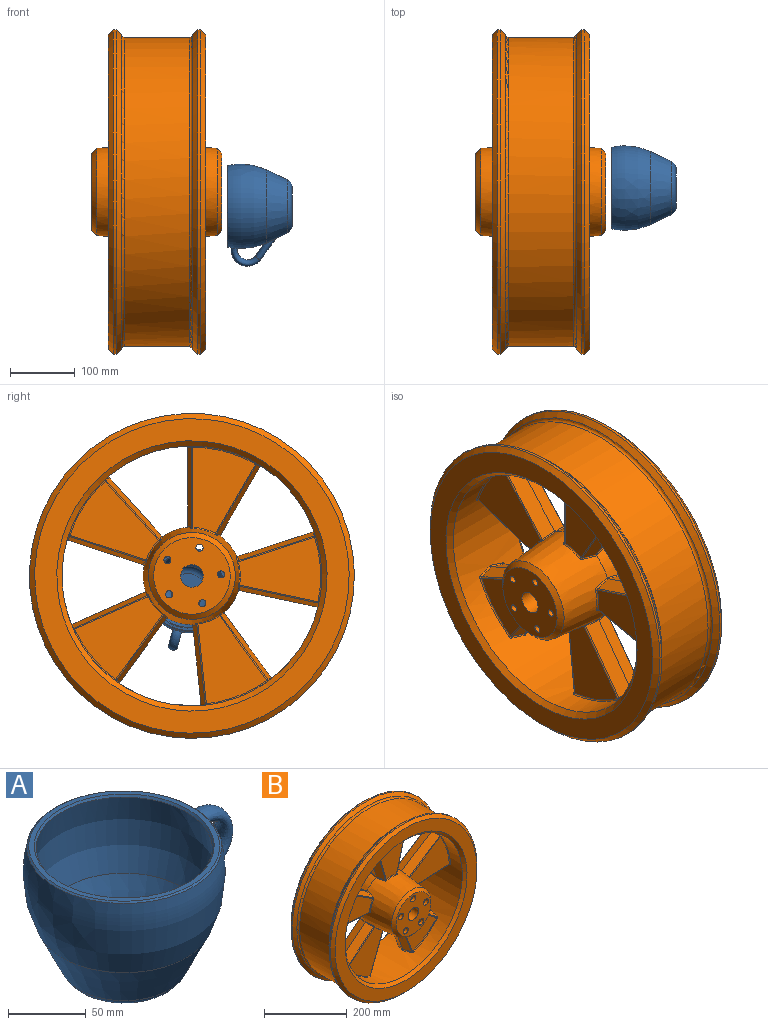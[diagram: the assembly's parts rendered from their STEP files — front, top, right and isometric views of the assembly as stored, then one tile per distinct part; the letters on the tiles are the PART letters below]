
ASSEMBLY  parts=2 mates=1
PART A: 13 faces, bbox 160.1x130.2x100 mm
  f0: revolved ~130.2x130.2mm, area 23793.2mm2, adj f3,f4,f5,f12
  f1: plane 122.99x122.99mm, normal (0,0,1), area 1330.6mm2, adj f11,f12
  f2: plane 59.81x59.81mm, normal (0,0,-1), area 2809.6mm2, adj f10
  f3: cone r=37.5mm half-angle=25.3deg, axis (0,0,1), area 10977.2mm2, adj f0,f4,f10
  f4: bspline ~41.94x33.4mm, area 1363.5mm2, adj f0,f3,f5
  f5: bspline ~45.43x33.49mm, area 2154.2mm2, adj f0,f4
  f6: revolved ~118.2x118.2mm, area 20523.6mm2, adj f8,f11
  f7: plane 52.22x52.22mm, normal (0,0,1), area 2141.3mm2, adj f9
  f8: cone r=33.7mm half-angle=25.3deg, axis (0,0,1), area 9083.2mm2, adj f6,f9
  f9: torus R=26.11mm, axis (0,0,1), area 2739mm2, adj f7,f8
  f10: torus R=29.91mm, axis (0,0,-1), area 3062.2mm2, adj f2,f3
  f11: cone r=56.71mm half-angle=38.1deg, axis (0,0,1), area 722.7mm2, adj f1,f6
  f12: cone r=62.74mm half-angle=51.6deg, axis (0,0,-1), area 618.7mm2, adj f0,f1
PART B: 186 faces, bbox 547x222x547 mm
  f0: cylinder r=250mm len=500mm, axis (0,1,0), area 6283.2mm2, adj f1,f185
  f1: cone r=250mm half-angle=45deg, axis (0,-1,0), area 17487.2mm2, adj f0,f2
  f2: plane 484x484mm, normal (0,1,0), area 48066.4mm2, adj f1,f3
  f3: cone r=208mm half-angle=45deg, axis (0,1,0), area 14501.6mm2, adj f2,f4
  f4: cylinder r=200mm len=400mm, axis (0,1,0), area 137396.1mm2, adj f3,f5,f128,f129,f130,f131,f132,f133
  f5: bspline ~4.6x3.93mm, area 11.3mm2, adj f4,f6,f128,f136
  f6: cylinder r=2mm len=119.66mm, axis (-0.26,0,-0.97), area 322.6mm2, adj f5,f7,f126,f127
  f7: plane 125.52x99.52mm, normal (0,1,0), area 8426.2mm2, adj f6,f8,f125,f128
  f8: cylinder r=2mm len=119.66mm, axis (-0.26,0,0.97), area 322.6mm2, adj f7,f9,f124,f129
  f9: plane 119x37.91mm, normal (-0.93,0.26,-0.25), area 2975.3mm2, adj f8,f10,f123,f130
  f10: plane 119x37.91mm, normal (-0.93,-0.26,-0.25), area 2975.3mm2, adj f9,f11,f122,f131
  f11: cylinder r=2mm len=119.66mm, axis (-0.26,0,0.97), area 322.6mm2, adj f10,f12,f121,f132
  f12: plane 125.52x99.52mm, normal (0,-1,0), area 8426.2mm2, adj f11,f13,f120,f133
  f13: cylinder r=2mm len=119.66mm, axis (-0.26,0,-0.97), area 322.6mm2, adj f12,f14,f119,f134
  f14: plane 119x37.91mm, normal (0.93,-0.26,-0.25), area 2975.3mm2, adj f13,f15,f127,f135
  f15: bspline ~24.26x7.79mm, area 72.3mm2, adj f14,f16,f118,f119
  f16: cone r=75mm half-angle=5deg, axis (0,1,0), area 34978.1mm2, adj f15,f17,f33,f34,f35,f36,f37,f53
  f17: bspline ~24.26x7.69mm, area 72.3mm2, adj f16,f18,f32,f33
  f18: plane 117.04x49.43mm, normal (0.9,-0.26,-0.35), area 2975.3mm2, adj f17,f19,f31,f150
  f19: cylinder r=2mm len=115.86mm, axis (-0.36,0,-0.93), area 322.6mm2, adj f18,f20,f33,f151
  f20: plane 136.13x124.73mm, normal (0,-1,0), area 8426.2mm2, adj f19,f21,f34,f152
  f21: cylinder r=2mm len=97.09mm, axis (0.78,0,0.63), area 322.6mm2, adj f20,f22,f35,f153
  f22: plane 99.51x81.37mm, normal (-0.61,-0.26,0.75), area 2975.3mm2, adj f21,f23,f36,f154
  f23: plane 99.51x81.37mm, normal (-0.61,0.26,0.75), area 2975.3mm2, adj f22,f24,f30,f155
  f24: cylinder r=2mm len=97.09mm, axis (0.78,0,0.63), area 322.6mm2, adj f23,f25,f29,f156
  f25: plane 136.13x124.73mm, normal (0,1,0), area 8426.2mm2, adj f24,f26,f28,f147
  f26: cylinder r=2mm len=115.86mm, axis (-0.36,0,-0.93), area 322.6mm2, adj f25,f27,f31,f148
  f27: bspline ~4.46x3.93mm, area 10.7mm2, adj f26,f28,f32,f77
  f28: torus R=74.65mm, axis (0,1,0), area 105.1mm2, adj f25,f27,f29,f77
  f29: bspline ~4.44x3.65mm, area 10.7mm2, adj f24,f28,f30,f77
  f30: bspline ~24.26x6.52mm, area 72.3mm2, adj f23,f29,f36,f77
  f31: plane 117.04x49.43mm, normal (0.9,0.26,-0.35), area 2975.3mm2, adj f18,f26,f32,f149
  f32: bspline ~24.26x7.69mm, area 72.3mm2, adj f17,f27,f31,f77
  f33: bspline ~4.66x3.65mm, area 10.7mm2, adj f16,f17,f19,f34
  f34: torus R=74.65mm, axis (0,-1,0), area 105.1mm2, adj f16,f20,f33,f35
  f35: bspline ~4.27x3.93mm, area 10.7mm2, adj f16,f21,f34,f36
  f36: bspline ~24.26x6.52mm, area 72.3mm2, adj f16,f22,f30,f35
  f37: bspline ~24.26x8.11mm, area 72.3mm2, adj f16,f38,f52,f53
  f38: plane 123.1x23.52mm, normal (-0.05,-0.26,-0.96), area 2975.3mm2, adj f37,f39,f51,f140
  f39: cylinder r=2mm len=123.3mm, axis (-1,0,0.05), area 322.6mm2, adj f38,f40,f53,f141
  f40: plane 134.22x101.11mm, normal (0,-1,0), area 8426.2mm2, adj f39,f41,f54,f142
  f41: cylinder r=2mm len=104.51mm, axis (0.84,0,-0.54), area 322.6mm2, adj f40,f42,f55,f143
  f42: plane 105.34x72.24mm, normal (0.53,-0.26,0.81), area 2975.3mm2, adj f41,f43,f56,f144
  f43: plane 105.34x72.24mm, normal (0.53,0.26,0.81), area 2975.3mm2, adj f42,f44,f50,f145
  f44: cylinder r=2mm len=104.51mm, axis (0.84,0,-0.54), area 322.6mm2, adj f43,f45,f49,f146
  f45: plane 134.22x101.11mm, normal (0,1,0), area 8426.2mm2, adj f44,f46,f48,f137
  f46: cylinder r=2mm len=123.3mm, axis (-1,0,0.05), area 322.6mm2, adj f45,f47,f51,f138
  f47: bspline ~4.26x3.93mm, area 10.7mm2, adj f46,f48,f52,f77
  f48: torus R=74.65mm, axis (0,1,0), area 105.1mm2, adj f45,f47,f49,f77
  f49: bspline ~4.11x3.79mm, area 10.7mm2, adj f44,f48,f50,f77
  f50: bspline ~24.26x6.91mm, area 72.3mm2, adj f43,f49,f56,f77
  f51: plane 123.1x23.52mm, normal (-0.05,0.26,-0.96), area 2975.3mm2, adj f38,f46,f52,f139
  f52: bspline ~24.26x8.11mm, area 72.3mm2, adj f37,f47,f51,f77
  f53: bspline ~4.69x3.65mm, area 10.7mm2, adj f16,f37,f39,f54
  f54: torus R=74.65mm, axis (0,-1,0), area 105.1mm2, adj f16,f40,f53,f55
  f55: bspline ~3.93x3.76mm, area 10.7mm2, adj f16,f41,f54,f56
  f56: bspline ~24.26x6.91mm, area 72.3mm2, adj f16,f42,f50,f55
  f57: bspline ~24.26x6.91mm, area 72.3mm2, adj f16,f58,f72,f73
  f58: plane 105.34x72.24mm, normal (-0.53,-0.26,0.81), area 2975.3mm2, adj f57,f59,f71,f170
  f59: cylinder r=2mm len=104.51mm, axis (0.84,0,0.54), area 322.6mm2, adj f58,f60,f73,f171
  f60: plane 134.22x101.11mm, normal (0,-1,0), area 8426.2mm2, adj f59,f61,f74,f172
  f61: cylinder r=2mm len=123.3mm, axis (-1,0,-0.05), area 322.6mm2, adj f60,f62,f75,f173
  f62: plane 123.1x23.52mm, normal (0.05,-0.26,-0.96), area 2975.3mm2, adj f61,f63,f76,f174
  f63: plane 123.1x23.52mm, normal (0.05,0.26,-0.96), area 2975.3mm2, adj f62,f64,f70,f175
  f64: cylinder r=2mm len=123.3mm, axis (-1,0,-0.05), area 322.6mm2, adj f63,f65,f69,f176
  f65: plane 134.22x101.11mm, normal (0,1,0), area 8426.2mm2, adj f64,f66,f68,f167
  f66: cylinder r=2mm len=104.51mm, axis (0.84,0,0.54), area 322.6mm2, adj f65,f67,f71,f168
  f67: bspline ~3.93x3.76mm, area 10.7mm2, adj f66,f68,f72,f77
  f68: torus R=74.65mm, axis (0,1,0), area 105.1mm2, adj f65,f67,f69,f77
  f69: bspline ~4.69x3.65mm, area 10.7mm2, adj f64,f68,f70,f77
  f70: bspline ~24.26x8.11mm, area 72.3mm2, adj f63,f69,f76,f77
  f71: plane 105.34x72.24mm, normal (-0.53,0.26,0.81), area 2975.3mm2, adj f58,f66,f72,f169
  f72: bspline ~24.26x6.91mm, area 72.3mm2, adj f57,f67,f71,f77
  f73: bspline ~4.11x3.79mm, area 10.7mm2, adj f16,f57,f59,f74
  f74: torus R=74.65mm, axis (0,-1,0), area 105.1mm2, adj f16,f60,f73,f75
  f75: bspline ~4.26x3.93mm, area 10.7mm2, adj f16,f61,f74,f76
  f76: bspline ~24.26x8.11mm, area 72.3mm2, adj f16,f62,f70,f75
  f77: cone r=75mm half-angle=5deg, axis (0,-1,0), area 34978.1mm2, adj f16,f27,f28,f29,f30,f32,f47,f48
  f78: bspline ~24.26x7.69mm, area 72.3mm2, adj f77,f79,f89,f116
  f79: plane 117.04x49.43mm, normal (-0.9,0.26,-0.35), area 2975.3mm2, adj f78,f80,f88,f165
  f80: cylinder r=2mm len=115.86mm, axis (-0.36,0,0.93), area 322.6mm2, adj f79,f81,f89,f166
  f81: plane 136.13x124.73mm, normal (0,1,0), area 8426.2mm2, adj f80,f82,f90,f157
  f82: cylinder r=2mm len=97.09mm, axis (0.78,0,-0.63), area 322.6mm2, adj f81,f83,f91,f158
  f83: plane 99.51x81.37mm, normal (0.61,0.26,0.75), area 2975.3mm2, adj f82,f84,f92,f159
  f84: plane 99.51x81.37mm, normal (0.61,-0.26,0.75), area 2975.3mm2, adj f83,f85,f112,f160
  f85: cylinder r=2mm len=97.09mm, axis (0.78,0,-0.63), area 322.6mm2, adj f84,f86,f113,f161
  f86: plane 136.13x124.73mm, normal (0,-1,0), area 8426.2mm2, adj f85,f87,f114,f162
  f87: cylinder r=2mm len=115.86mm, axis (-0.36,0,0.93), area 322.6mm2, adj f86,f88,f115,f163
  f88: plane 117.04x49.43mm, normal (-0.9,-0.26,-0.35), area 2975.3mm2, adj f79,f87,f116,f164
  f89: bspline ~4.66x3.65mm, area 10.7mm2, adj f77,f78,f80,f90
  f90: torus R=74.65mm, axis (0,1,0), area 105.1mm2, adj f77,f81,f89,f91
  f91: bspline ~4.27x3.93mm, area 10.7mm2, adj f77,f82,f90,f92
  f92: bspline ~24.26x6.52mm, area 72.3mm2, adj f77,f83,f91,f112
  f93: cone r=66.89mm half-angle=47.5deg, axis (0,-1,0), area 4272.4mm2, adj f77,f94
  f94: plane 139.84x139.84mm, normal (0,1,0), area 9469.1mm2, adj f93,f95,f107,f108,f109,f110,f111
  f95: cylinder r=17.5mm len=200mm, axis (0,-1,0), area 21991.1mm2, adj f94,f96
  f96: plane 117.84x117.84mm, normal (0,-1,0), area 8775.8mm2, adj f95,f97,f99,f101,f103,f105,f117
  f97: cylinder r=8.62mm len=17.25mm, axis (0,-1,0), area 541.9mm2, adj f96,f98
  f98: plane 17.25x17.25mm, normal (0,-1,0), area 138.7mm2, adj f97,f107
  f99: cylinder r=8.62mm len=17.25mm, axis (0,-1,0), area 541.9mm2, adj f96,f100
  f100: plane 17.25x17.25mm, normal (0,-1,0), area 138.7mm2, adj f99,f108
  f101: cylinder r=8.62mm len=17.25mm, axis (0,-1,0), area 541.9mm2, adj f96,f102
  f102: plane 17.25x17.25mm, normal (0,-1,0), area 138.7mm2, adj f101,f109
  f103: cylinder r=8.62mm len=17.25mm, axis (0,-1,0), area 541.9mm2, adj f96,f104
  f104: plane 17.25x17.25mm, normal (0,-1,0), area 138.7mm2, adj f103,f110
  f105: cylinder r=8.62mm len=17.25mm, axis (0,-1,0), area 541.9mm2, adj f96,f106
  f106: plane 17.25x17.25mm, normal (0,-1,0), area 138.7mm2, adj f105,f111
  f107: cylinder r=5.5mm len=190mm, axis (0,-1,0), area 6565.9mm2, adj f94,f98
  f108: cylinder r=5.5mm len=190mm, axis (0,-1,0), area 13131.9mm2, adj f94,f100
  f109: cylinder r=5.5mm len=190mm, axis (0,-1,0), area 6565.9mm2, adj f94,f102
  f110: cylinder r=5.5mm len=190mm, axis (0,-1,0), area 6565.9mm2, adj f94,f104
  f111: cylinder r=5.5mm len=190mm, axis (0,-1,0), area 6565.9mm2, adj f94,f106
  f112: bspline ~24.26x6.52mm, area 72.3mm2, adj f16,f84,f92,f113
  f113: bspline ~4.44x3.65mm, area 10.7mm2, adj f16,f85,f112,f114
  f114: torus R=74.65mm, axis (0,-1,0), area 105.1mm2, adj f16,f86,f113,f115
  f115: bspline ~4.46x3.93mm, area 10.7mm2, adj f16,f87,f114,f116
  f116: bspline ~24.26x7.69mm, area 72.3mm2, adj f16,f78,f88,f115
  f117: cone r=58.92mm half-angle=47.5deg, axis (0,1,0), area 4272.4mm2, adj f16,f96
  f118: bspline ~24.26x7.79mm, area 72.3mm2, adj f15,f77,f126,f127
  f119: bspline ~4.22x3.93mm, area 10.7mm2, adj f13,f15,f16,f120
  f120: torus R=74.65mm, axis (0,-1,0), area 105.1mm2, adj f12,f16,f119,f121
  f121: bspline ~4.63x3.65mm, area 10.7mm2, adj f11,f16,f120,f122
  f122: bspline ~24.26x7.79mm, area 72.3mm2, adj f10,f16,f121,f123
  f123: bspline ~24.26x7.79mm, area 72.3mm2, adj f9,f77,f122,f124
  f124: bspline ~4.22x3.93mm, area 10.7mm2, adj f8,f77,f123,f125
  f125: torus R=74.65mm, axis (0,1,0), area 105.1mm2, adj f7,f77,f124,f126
  f126: bspline ~4.63x3.65mm, area 10.7mm2, adj f6,f77,f118,f125
  f127: plane 119x37.91mm, normal (0.93,0.26,-0.25), area 2975.3mm2, adj f6,f14,f118,f136
  f128: torus R=198mm, axis (0,1,0), area 318.1mm2, adj f4,f5,f7,f129
  f129: bspline ~4.79x3.68mm, area 11.3mm2, adj f4,f8,f128,f130
  f130: bspline ~81.1x23.21mm, area 78.6mm2, adj f4,f9,f129,f131
  f131: bspline ~81.1x23.21mm, area 78.6mm2, adj f4,f10,f130,f132
  f132: bspline ~4.6x3.93mm, area 11.3mm2, adj f4,f11,f131,f133
  f133: torus R=198mm, axis (0,-1,0), area 318.1mm2, adj f4,f12,f132,f134
  f134: bspline ~4.79x3.68mm, area 11.3mm2, adj f4,f13,f133,f135
  f135: bspline ~81.1x23.21mm, area 78.6mm2, adj f4,f14,f134,f136
  f136: bspline ~81.1x23.21mm, area 78.6mm2, adj f4,f5,f127,f135
  f137: torus R=198mm, axis (0,1,0), area 318.1mm2, adj f4,f45,f138,f146
  f138: bspline ~4.89x3.68mm, area 11.3mm2, adj f4,f46,f137,f139
  f139: bspline ~81.1x23.7mm, area 78.6mm2, adj f4,f51,f138,f140
  f140: bspline ~81.1x23.7mm, area 78.6mm2, adj f4,f38,f139,f141
  f141: bspline ~4.43x3.93mm, area 11.3mm2, adj f4,f39,f140,f142
  f142: torus R=198mm, axis (0,-1,0), area 318.1mm2, adj f4,f40,f141,f143
  f143: bspline ~4.8x3.68mm, area 11.3mm2, adj f4,f41,f142,f144
  f144: bspline ~81.1x20.57mm, area 78.6mm2, adj f4,f42,f143,f145
  f145: bspline ~81.1x20.57mm, area 78.6mm2, adj f4,f43,f144,f146
  f146: bspline ~4.56x3.6mm, area 11.3mm2, adj f4,f44,f137,f145
  f147: torus R=198mm, axis (0,1,0), area 318.1mm2, adj f4,f25,f148,f156
  f148: bspline ~4.57x3.68mm, area 11.3mm2, adj f4,f26,f147,f149
  f149: bspline ~24.55x7.38mm, area 78.6mm2, adj f4,f31,f148,f150
  f150: bspline ~24.55x7.38mm, area 78.6mm2, adj f4,f18,f149,f151
  f151: bspline ~4.07x3.6mm, area 11.3mm2, adj f4,f19,f150,f152
  f152: torus R=198mm, axis (0,-1,0), area 318.1mm2, adj f4,f20,f151,f153
  f153: bspline ~4.34x3.8mm, area 11.3mm2, adj f4,f21,f152,f154
  f154: bspline ~81.1x18.84mm, area 78.6mm2, adj f4,f22,f153,f155
  f155: bspline ~81.1x18.84mm, area 78.6mm2, adj f4,f23,f154,f156
  f156: bspline ~4.21x3.93mm, area 11.3mm2, adj f4,f24,f147,f155
  f157: torus R=198mm, axis (0,1,0), area 318.1mm2, adj f4,f81,f158,f166
  f158: bspline ~4.34x3.8mm, area 11.3mm2, adj f4,f82,f157,f159
  f159: bspline ~81.1x18.84mm, area 78.6mm2, adj f4,f83,f158,f160
  f160: bspline ~81.1x18.84mm, area 78.6mm2, adj f4,f84,f159,f161
  f161: bspline ~4.21x3.93mm, area 11.3mm2, adj f4,f85,f160,f162
  f162: torus R=198mm, axis (0,-1,0), area 318.1mm2, adj f4,f86,f161,f163
  f163: bspline ~4.57x3.68mm, area 11.3mm2, adj f4,f87,f162,f164
  f164: bspline ~24.55x7.38mm, area 78.6mm2, adj f4,f88,f163,f165
  f165: bspline ~24.55x7.38mm, area 78.6mm2, adj f4,f79,f164,f166
  f166: bspline ~4.07x3.6mm, area 11.3mm2, adj f4,f80,f157,f165
  f167: torus R=198mm, axis (0,1,0), area 318.1mm2, adj f4,f65,f168,f176
  f168: bspline ~4.8x3.68mm, area 11.3mm2, adj f4,f66,f167,f169
  f169: bspline ~81.1x20.57mm, area 78.6mm2, adj f4,f71,f168,f170
  f170: bspline ~81.1x20.57mm, area 78.6mm2, adj f4,f58,f169,f171
  f171: bspline ~4.56x3.6mm, area 11.3mm2, adj f4,f59,f170,f172
  f172: torus R=198mm, axis (0,-1,0), area 318.1mm2, adj f4,f60,f171,f173
  f173: bspline ~4.89x3.68mm, area 11.3mm2, adj f4,f61,f172,f174
  f174: bspline ~81.1x23.7mm, area 78.6mm2, adj f4,f62,f173,f175
  f175: bspline ~81.1x23.7mm, area 78.6mm2, adj f4,f63,f174,f176
  f176: bspline ~4.43x3.93mm, area 11.3mm2, adj f4,f64,f167,f175
  f177: cone r=200mm half-angle=45deg, axis (0,-1,0), area 14501.6mm2, adj f4,f178
  f178: plane 484x484mm, normal (0,-1,0), area 48066.4mm2, adj f177,f179
  f179: cone r=242mm half-angle=45deg, axis (0,1,0), area 17487.2mm2, adj f178,f180
  f180: cylinder r=250mm len=500mm, axis (0,1,0), area 6283.2mm2, adj f179,f181
  f181: cone r=250mm half-angle=45deg, axis (0,-1,0), area 17487.2mm2, adj f180,f182
  f182: torus R=242.5mm, axis (0,-1,0), area 11047.5mm2, adj f181,f183
  f183: cylinder r=237.5mm len=475mm, axis (0,1,0), area 149300.5mm2, adj f182,f184
  f184: torus R=242.5mm, axis (0,1,0), area 11047.5mm2, adj f183,f185
  f185: cone r=242mm half-angle=45deg, axis (0,1,0), area 17487.2mm2, adj f0,f184
PLACE A rot(axis=(-0.7,-0.09,0.7),169.4deg) t=(207.86,5.95,-22.22)mm
PLACE B rot(axis=(0.13,-0.13,0.98),91deg) t=(0,0,0)mm fixed
MATE slider A.f3 <-> B.f96  axis (-1,0,0) through (107.86,5.95,-22.22)mm
